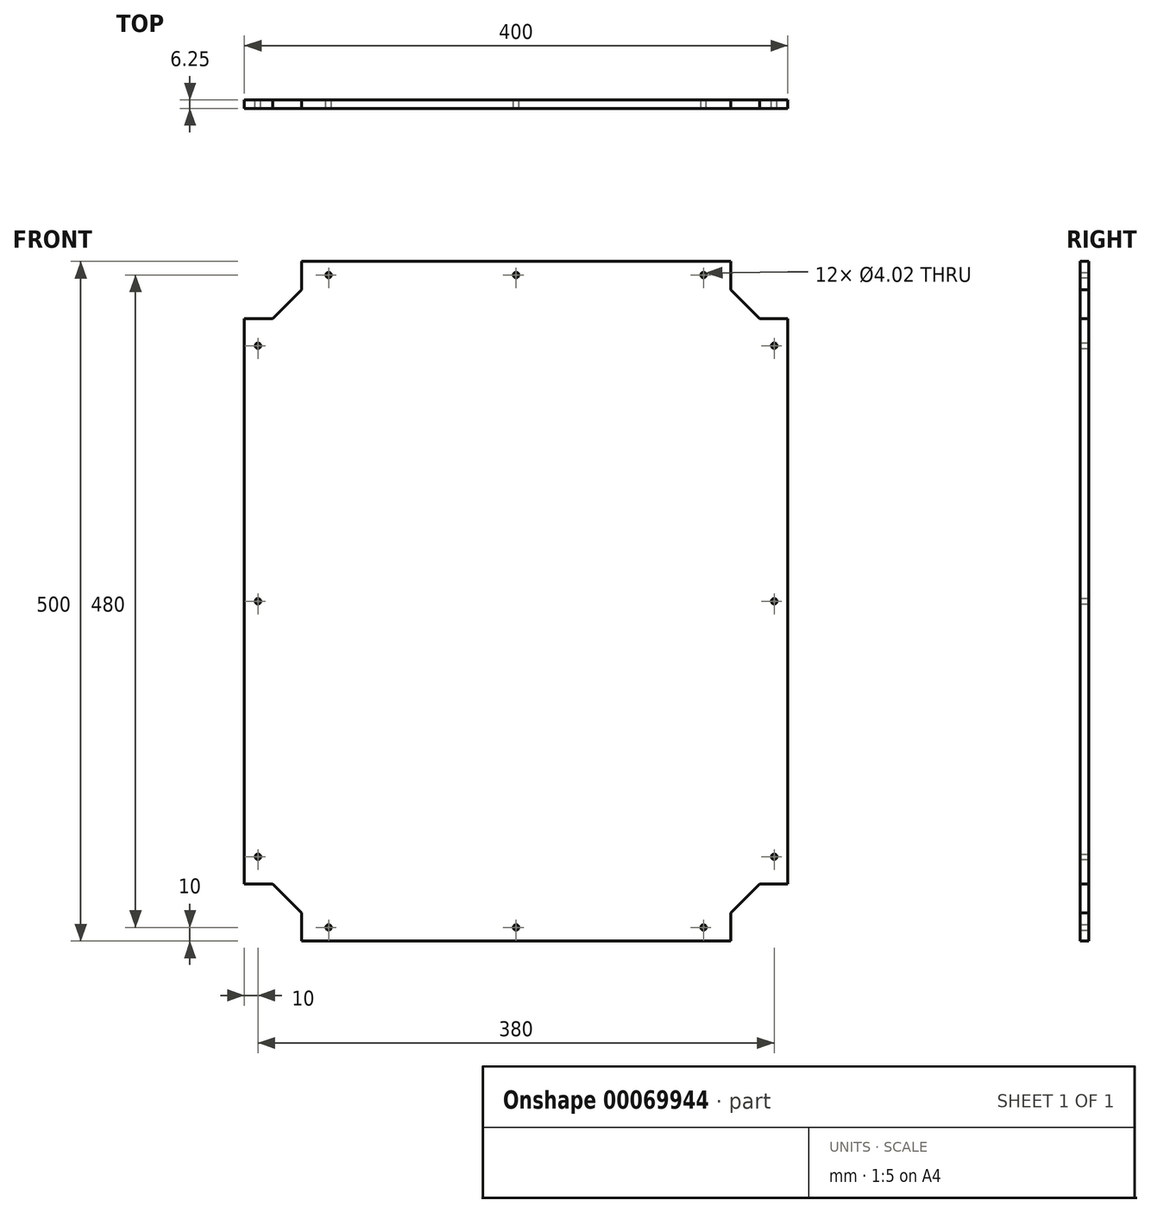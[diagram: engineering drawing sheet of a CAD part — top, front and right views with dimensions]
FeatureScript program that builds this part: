
annotation { "Feature Type Name" : "Feature", "Feature Type Description" : "" }
export const myFeature = defineFeature(function(context is Context, id is Id, definition is map)
    precondition{}
    {
        {
            var Q0;
            Q0=qCreatedBy(makeId("Front.planeOp"),FACE);
            var sketch = newSketch(context, id + "F0", { "sketchPlane" : qUnion([Q0])});
            skLineSegment(sketch, "E0", {"start": v(0, 0) * mm, "end": v(180, 0) * mm, "construction": true});
            skLineSegment(sketch, "E1", {"start": v(0, 0) * mm, "end": v(0, -230) * mm, "construction": true});
            skLineSegment(sketch, "E2", {"start": v(0, 0) * mm, "end": v(-180, 0) * mm, "construction": true});
            skLineSegment(sketch, "E3", {"start": v(0, 0) * mm, "end": v(0, 230) * mm, "construction": true});
            skLineSegment(sketch, "E4", {"start": v(0, 230) * mm, "end": v(160, 230) * mm, "construction": true});
            skLineSegment(sketch, "E5", {"start": v(0, 230) * mm, "end": v(-160, 230) * mm, "construction": true});
            skLineSegment(sketch, "E6", {"start": v(0, -230) * mm, "end": v(160, -230) * mm, "construction": true});
            skLineSegment(sketch, "E7", {"start": v(0, -230) * mm, "end": v(-160, -230) * mm, "construction": true});
            skLineSegment(sketch, "E8", {"start": v(-180, 0) * mm, "end": v(-180, -210) * mm, "construction": true});
            skLineSegment(sketch, "E9", {"start": v(-180, 0) * mm, "end": v(-180, 210) * mm, "construction": true});
            skLineSegment(sketch, "E10", {"start": v(180, 0) * mm, "end": v(180, 210) * mm, "construction": true});
            skLineSegment(sketch, "E11", {"start": v(180, 0) * mm, "end": v(180, -210) * mm, "construction": true});
            skLineSegment(sketch, "E12", {"start": v(-180, 210) * mm, "end": v(-160, 230) * mm, "construction": true});
            skLineSegment(sketch, "E13", {"start": v(160, 230) * mm, "end": v(180, 210) * mm, "construction": true});
            skLineSegment(sketch, "E14", {"start": v(-180, -210) * mm, "end": v(-160, -230) * mm, "construction": true});
            skLineSegment(sketch, "E15", {"start": v(160, -230) * mm, "end": v(180, -210) * mm, "construction": true});
            skLineSegment(sketch, "E16", {"start": v(140, 230) * mm, "end": v(140, 185) * mm, "construction": true});
            skLineSegment(sketch, "E17", {"start": v(140, 185) * mm, "end": v(180, 185) * mm, "construction": true});
            skLineSegment(sketch, "E18", {"start": v(-140, 230) * mm, "end": v(-140, 185) * mm, "construction": true});
            skLineSegment(sketch, "E19", {"start": v(-140, 185) * mm, "end": v(-180, 185) * mm, "construction": true});
            skLineSegment(sketch, "E20", {"start": v(170, 220) * mm, "end": v(168.59, 218.59) * mm, "construction": true});
            skLineSegment(sketch, "E21", {"start": v(180, 210) * mm, "end": v(200, 210) * mm, "construction": true});
            skLineSegment(sketch, "E22", {"start": v(190, 210) * mm, "end": v(190, 208) * mm, "construction": true});
            skLineSegment(sketch, "E23", {"start": v(160, 230) * mm, "end": v(160, 250) * mm, "construction": true});
            skLineSegment(sketch, "E24", {"start": v(180, -210) * mm, "end": v(200, -210) * mm, "construction": true});
            skLineSegment(sketch, "E25", {"start": v(160, -230) * mm, "end": v(160, -250) * mm, "construction": true});
            skLineSegment(sketch, "E26", {"start": v(-180, -210) * mm, "end": v(-200, -210) * mm, "construction": true});
            skLineSegment(sketch, "E27", {"start": v(-160, -230) * mm, "end": v(-160, -250) * mm, "construction": true});
            skLineSegment(sketch, "E28", {"start": v(190, -210) * mm, "end": v(190, -208) * mm, "construction": true});
            skLineSegment(sketch, "E29", {"start": v(160, -240) * mm, "end": v(158, -240) * mm, "construction": true});
            skLineSegment(sketch, "E30", {"start": v(190, -208) * mm, "end": v(200, -208) * mm});
            skLineSegment(sketch, "E31", {"start": v(170, -220) * mm, "end": v(168.59, -218.59) * mm, "construction": true});
            skLineSegment(sketch, "E32", {"start": v(190, -208) * mm, "end": v(179.17, -208) * mm});
            skLineSegment(sketch, "E33", {"start": v(168.59, -218.59) * mm, "end": v(179.17, -208) * mm});
            skLineSegment(sketch, "E34", {"start": v(168.59, -218.59) * mm, "end": v(158, -229.17) * mm});
            skLineSegment(sketch, "E35", {"start": v(158, -240) * mm, "end": v(158, -229.17) * mm});
            skLineSegment(sketch, "E36", {"start": v(158, -240) * mm, "end": v(158, -250) * mm});
            skLineSegment(sketch, "E37", {"start": v(200, -208) * mm, "end": v(200, 208) * mm});
            skLineSegment(sketch, "E38", {"start": v(200, 208) * mm, "end": v(190, 208) * mm});
            skLineSegment(sketch, "E39", {"start": v(190, 208) * mm, "end": v(179.17, 208) * mm});
            skLineSegment(sketch, "E40", {"start": v(168.59, 218.59) * mm, "end": v(179.17, 208) * mm});
            skLineSegment(sketch, "E41", {"start": v(168.59, 218.59) * mm, "end": v(158, 229.17) * mm});
            skLineSegment(sketch, "E42", {"start": v(160, 240) * mm, "end": v(158, 240) * mm, "construction": true});
            skPoint(sketch, "E42.endSnap0", {"position": v(160, 240) * mm});
            skLineSegment(sketch, "E43", {"start": v(158, 240) * mm, "end": v(158, 229.17) * mm});
            skLineSegment(sketch, "E44", {"start": v(-160, -240) * mm, "end": v(-158, -240) * mm, "construction": true});
            skLineSegment(sketch, "E45", {"start": v(-170, -220) * mm, "end": v(-168.59, -218.59) * mm, "construction": true});
            skLineSegment(sketch, "E46", {"start": v(-190, -210) * mm, "end": v(-190, -208) * mm, "construction": true});
            skPoint(sketch, "E46.endSnap0", {"position": v(-190, -210) * mm});
            skLineSegment(sketch, "E47", {"start": v(-168.59, -218.59) * mm, "end": v(-157.17, -230) * mm});
            skLineSegment(sketch, "E48", {"start": v(-158, -240) * mm, "end": v(-158, -229.17) * mm});
            skLineSegment(sketch, "E49", {"start": v(-190, -208) * mm, "end": v(-179.17, -208) * mm});
            skLineSegment(sketch, "E50", {"start": v(-168.59, -218.59) * mm, "end": v(-179.17, -208) * mm});
            skLineSegment(sketch, "E51", {"start": v(-158, -240) * mm, "end": v(-158, -250) * mm});
            skLineSegment(sketch, "E52", {"start": v(-190, -208) * mm, "end": v(-200, -208) * mm});
            skLineSegment(sketch, "E53", {"start": v(-158, -250) * mm, "end": v(158, -250) * mm});
            skLineSegment(sketch, "E54", {"start": v(-160, 230) * mm, "end": v(-160, 250) * mm, "construction": true});
            skLineSegment(sketch, "E55", {"start": v(-180, 210) * mm, "end": v(-200, 210) * mm, "construction": true});
            skLineSegment(sketch, "E56", {"start": v(-160, 240) * mm, "end": v(-158, 240) * mm, "construction": true});
            skLineSegment(sketch, "E57", {"start": v(-170, 220) * mm, "end": v(-168.59, 218.59) * mm, "construction": true});
            skLineSegment(sketch, "E58", {"start": v(-190, 210) * mm, "end": v(-190, 208) * mm, "construction": true});
            skLineSegment(sketch, "E59", {"start": v(-190, 208) * mm, "end": v(-200, 208) * mm});
            skLineSegment(sketch, "E60", {"start": v(-200, 208) * mm, "end": v(-200, -208) * mm});
            skLineSegment(sketch, "E61", {"start": v(-190, 208) * mm, "end": v(-179.17, 208) * mm});
            skLineSegment(sketch, "E62", {"start": v(-168.59, 218.59) * mm, "end": v(-179.17, 208) * mm});
            skLineSegment(sketch, "E63", {"start": v(-168.59, 218.59) * mm, "end": v(-158, 229.17) * mm});
            skLineSegment(sketch, "E64", {"start": v(-158, 240) * mm, "end": v(-158, 229.17) * mm});
            skLineSegment(sketch, "E65", {"start": v(-158, 240) * mm, "end": v(-158, 250) * mm});
            skLineSegment(sketch, "E66", {"start": v(-158, 250) * mm, "end": v(158, 250) * mm});
            skLineSegment(sketch, "E67", {"start": v(158, 250) * mm, "end": v(158, 240) * mm});
            skLineSegment(sketch, "E68", {"start": v(158, 240) * mm, "end": v(-158, 240) * mm, "construction": true});
            skLineSegment(sketch, "E69", {"start": v(-190, 208) * mm, "end": v(-190, -208) * mm, "construction": true});
            skLineSegment(sketch, "E70", {"start": v(-158, -240) * mm, "end": v(158, -240) * mm, "construction": true});
            skLineSegment(sketch, "E71", {"start": v(190, -208) * mm, "end": v(190, 208) * mm, "construction": true});
            skLineSegment(sketch, "E72", {"start": v(-168.59, 218.59) * mm, "end": v(-129.7, 179.7) * mm, "construction": true});
            skLineSegment(sketch, "E73", {"start": v(168.59, 218.59) * mm, "end": v(129.7, 179.7) * mm, "construction": true});
            skLineSegment(sketch, "E74", {"start": v(160, 165) * mm, "end": v(180, 165) * mm, "construction": true});
            skLineSegment(sketch, "E75", {"start": v(-160, 165) * mm, "end": v(-180, 165) * mm, "construction": true});
            skCircle(sketch, "E76", {"center": v(0, -240) * mm, "radius": 2 * mm});
            skCircle(sketch, "E77", {"center": v(138, -240) * mm, "radius": 2 * mm});
            skCircle(sketch, "E78", {"center": v(-138, -240) * mm, "radius": 2 * mm});
            skCircle(sketch, "E79", {"center": v(190, -188) * mm, "radius": 2 * mm});
            skCircle(sketch, "E80", {"center": v(190, 0) * mm, "radius": 2 * mm});
            skCircle(sketch, "E81", {"center": v(190, 188) * mm, "radius": 2 * mm});
            skCircle(sketch, "E82", {"center": v(0, 240) * mm, "radius": 2 * mm});
            skCircle(sketch, "E83", {"center": v(138, 240) * mm, "radius": 2 * mm});
            skCircle(sketch, "E84", {"center": v(-138, 240) * mm, "radius": 2 * mm});
            skCircle(sketch, "E85", {"center": v(-190, 188) * mm, "radius": 2 * mm});
            skCircle(sketch, "E86", {"center": v(-190, 0) * mm, "radius": 2 * mm});
            skCircle(sketch, "E87", {"center": v(-190, -188) * mm, "radius": 2 * mm});
            skSolve(sketch);
        }
        {
            var Q0;
            Q0=makeQuery(id+"F0.imprint","IMPRINT",FACE,{"disambiguationData":[TD([[makeQuery(id+"F0.imprint","IMPRINT",EDGE,{"derivedFrom":sQuery(id+"F0.wireOp",EDGE,"E30")}),1.0]])]});
            var Q1;
            Q1=qSketchRegion(id+"F0",true);
            extrude(context, id + "F1", {"entities" : qUnion([Q0, Q1]), "depth" : 6.25 * mm});
        }
    });
